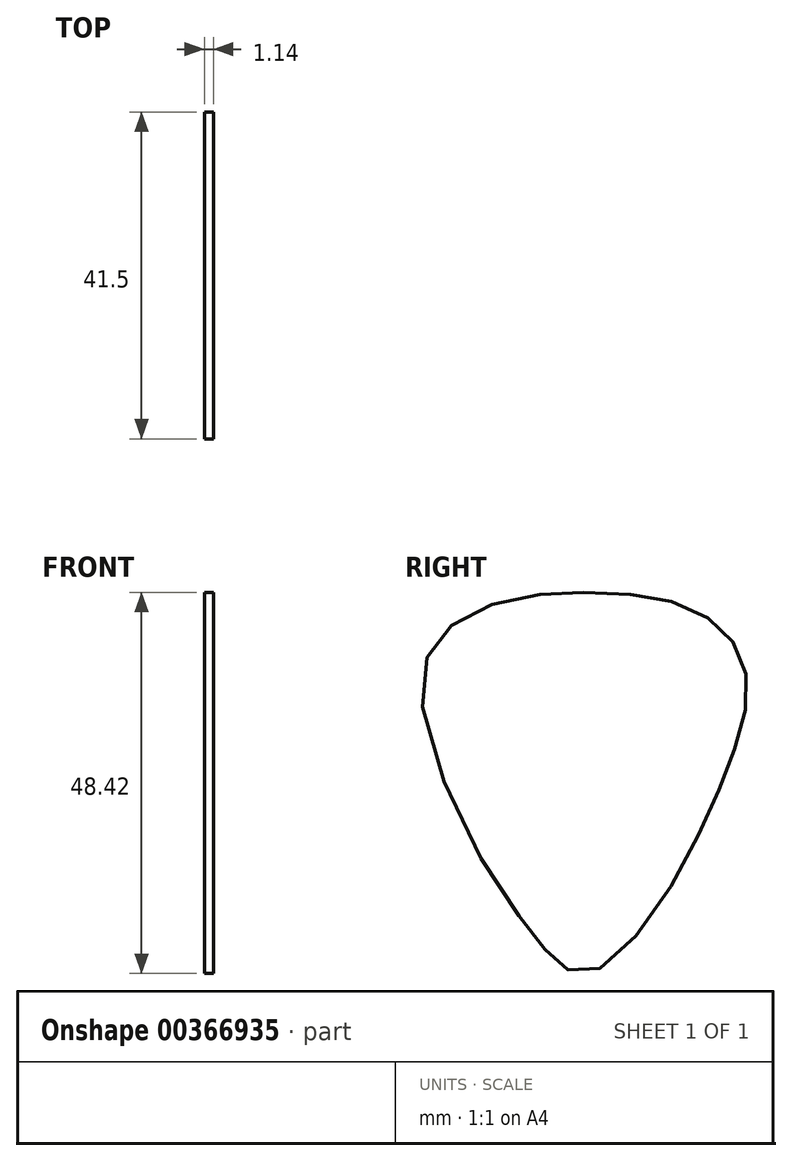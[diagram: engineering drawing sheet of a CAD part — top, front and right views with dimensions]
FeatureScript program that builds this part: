
annotation { "Feature Type Name" : "Feature", "Feature Type Description" : "" }
export const myFeature = defineFeature(function(context is Context, id is Id, definition is map)
    precondition{}
    {
        {
            var Q0;
            Q0=qCreatedBy(makeId("Right.planeOp"),FACE);
            var sketch = newSketch(context, id + "F0", { "sketchPlane" : qUnion([Q0])});
            skFitSpline(sketch, "E0", {"points": [v(-18.46, 29.96) * mm, v(-11.04, 29.55) * mm, v(-5.68, 28.21) * mm, v(-1.04, 25.53) * mm, v(1.13, 22.54) * mm, v(2.36, 18.42) * mm, v(1.85, 13.78) * mm, v(0, 8) * mm, v(-2.8, 1.4) * mm, v(-8.05, -8.5) * mm, v(-15.06, -16.95) * mm, v(-19.11, -18.42) * mm, v(-22.19, -16.74) * mm, v(-24.26, -14.21) * mm, v(-31.4, -4.03) * mm, v(-39.04, 16.5) * mm, v(-37.44, 23.36) * mm, v(-32.98, 27.22) * mm, v(-25.12, 29.53) * mm, v(-18.46, 29.96) * mm]});
            skSolve(sketch);
        }
        {
            var Q0;
            Q0 = qSketchRegion(id + "F0", true);
            extrude(context, id + "F1", {"entities" : qUnion([Q0]), "depth" : 1.14 * mm});
        }
    });
